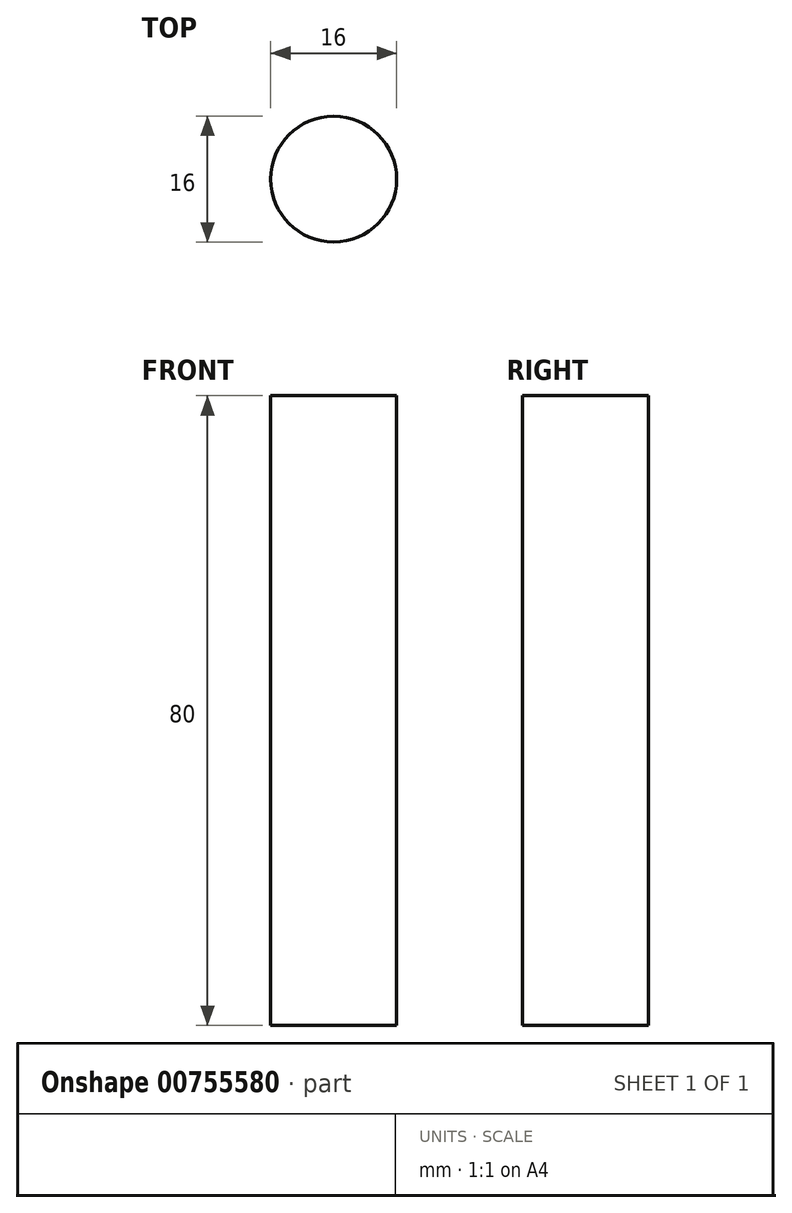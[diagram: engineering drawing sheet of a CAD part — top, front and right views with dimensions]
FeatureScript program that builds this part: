
annotation { "Feature Type Name" : "Feature", "Feature Type Description" : "" }
export const myFeature = defineFeature(function(context is Context, id is Id, definition is map)
    precondition{}
    {
        {
            var Q0;
            Q0=qCreatedBy(makeId("Top.planeOp"),FACE);
            var sketch = newSketch(context, id + "F0", { "sketchPlane" : qUnion([Q0])});
            skCircle(sketch, "E0", {"center": v(0, 0) * mm, "radius": 8 * mm});
            skSolve(sketch);
        }
        {
            var Q0;
            Q0=qSketchRegion(id+"F0",true);
            extrude(context, id + "F1", {"entities" : qUnion([Q0]), "depth" : 80 * mm, "offsetDistance" : 25 * mm});
        }
    });
